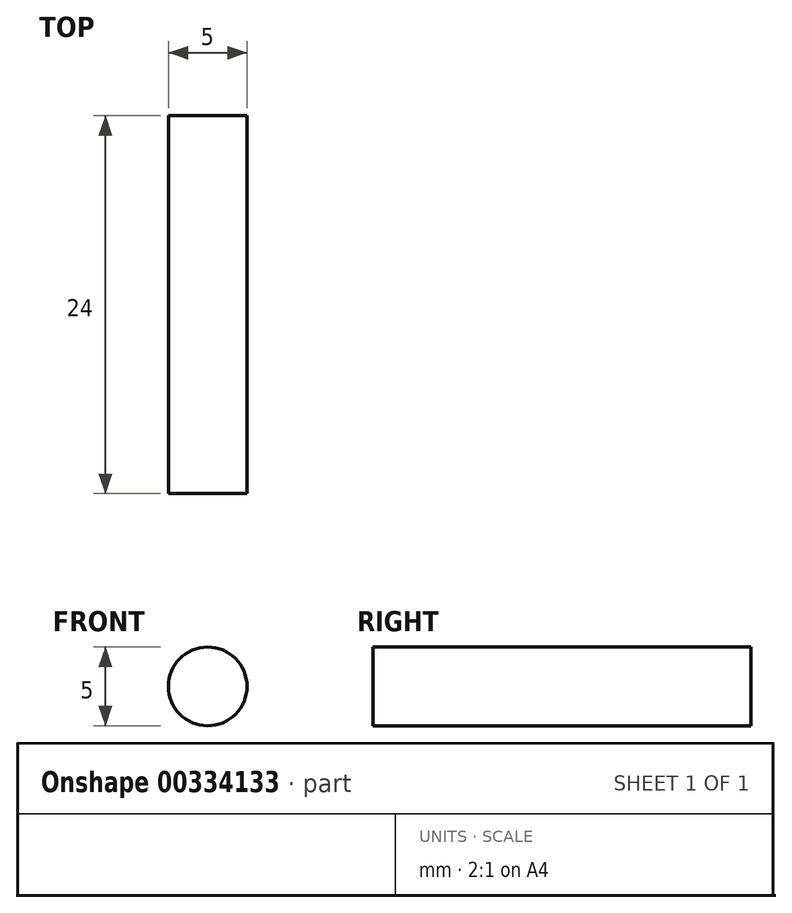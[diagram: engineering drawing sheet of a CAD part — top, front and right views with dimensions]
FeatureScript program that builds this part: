
annotation { "Feature Type Name" : "Feature", "Feature Type Description" : "" }
export const myFeature = defineFeature(function(context is Context, id is Id, definition is map)
    precondition{}
    {
        {
            var Q0;
            Q0=qCreatedBy(makeId("Front.planeOp"),FACE);
            var sketch = newSketch(context, id + "F0", { "sketchPlane" : qUnion([Q0])});
            skCircle(sketch, "E0", {"center": v(0, 0) * mm, "radius": 2.5 * mm});
            skSolve(sketch);
        }
        {
            var Q0;
            Q0 = qSketchRegion(id + "F0", true);
            extrude(context, id + "F1", {"entities" : qUnion([Q0]), "depth" : 24 * mm});
        }
    });
